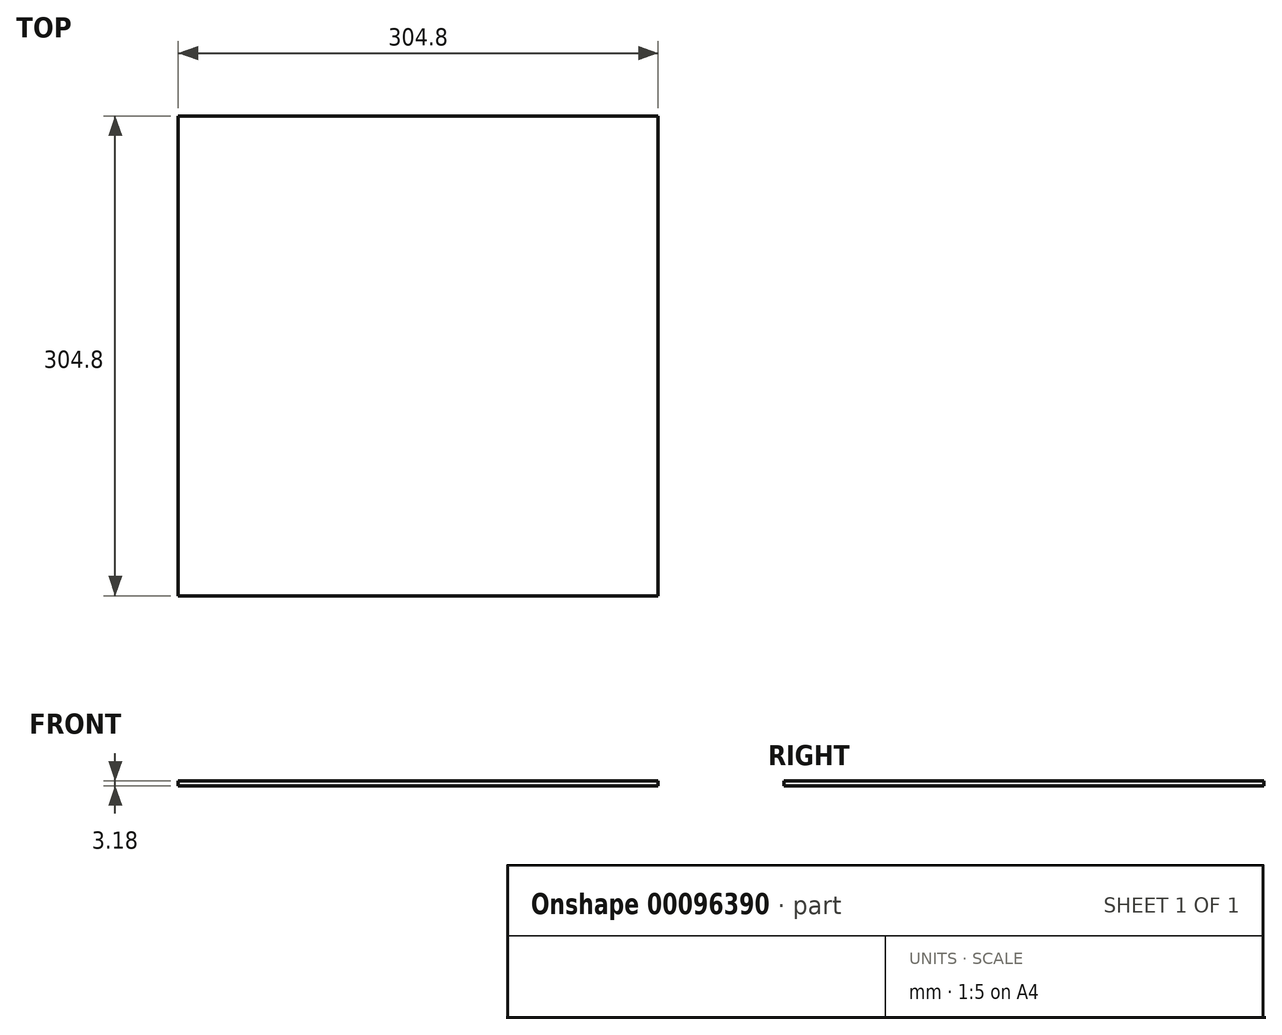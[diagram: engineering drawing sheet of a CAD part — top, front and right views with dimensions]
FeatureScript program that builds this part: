
annotation { "Feature Type Name" : "Feature", "Feature Type Description" : "" }
export const myFeature = defineFeature(function(context is Context, id is Id, definition is map)
    precondition{}
    {
        {
            var Q0;
            Q0=qCreatedBy(makeId("Top.planeOp"),FACE);
            var sketch = newSketch(context, id + "F0", { "sketchPlane" : qUnion([Q0])});
            skLineSegment(sketch, "E0.bottom", {"start": v(152.4, -152.4) * mm, "end": v(-152.4, -152.4) * mm});
            skLineSegment(sketch, "E0.top", {"start": v(152.4, 152.4) * mm, "end": v(-152.4, 152.4) * mm});
            skLineSegment(sketch, "E0.left", {"start": v(152.4, -152.4) * mm, "end": v(152.4, 152.4) * mm});
            skLineSegment(sketch, "E0.right", {"start": v(-152.4, -152.4) * mm, "end": v(-152.4, 152.4) * mm});
            skPoint(sketch, "E0.middle", {"position": v(0, 0) * mm});
            skSolve(sketch);
        }
        {
            var Q0;
            Q0=makeQuery(id+"F0.imprint","IMPRINT",FACE,{"disambiguationData":[TD([[makeQuery(id+"F0.imprint","IMPRINT",EDGE,{"derivedFrom":sQuery(id+"F0.wireOp",EDGE,"E0.bottom")}),-1.0]])]});
            extrude(context, id + "F1", {"entities" : qUnion([Q0]), "endBound" : BoundingType.SYMMETRIC, "depth" : 3.17 * mm});
        }
    });
